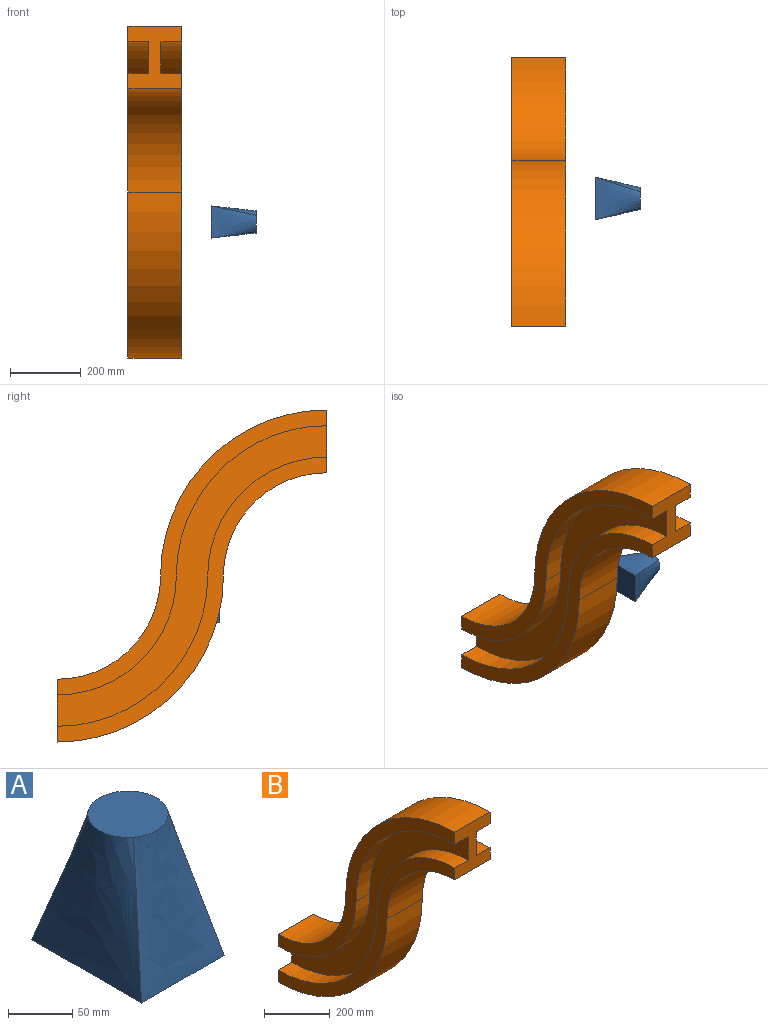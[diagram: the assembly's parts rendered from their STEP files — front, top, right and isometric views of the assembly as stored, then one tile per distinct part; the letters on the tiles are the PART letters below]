
ASSEMBLY  parts=2 mates=1
PART A: 6 faces, bbox 91.2x120.9x127 mm
  f0: plane 120.89x91.17mm, normal (0,0,-1), area 11021.7mm2, adj f2,f3,f4,f5
  f1: plane 62.63x62.63mm, normal (0,0,1), area 3078mm2, adj f2,f3,f4,f5
  f2: bspline ~127x91.17mm, area 9063.2mm2, adj f0,f1,f3,f5
  f3: bspline ~127x120.89mm, area 10768.1mm2, adj f0,f1,f2,f4
  f4: bspline ~127x91.17mm, area 9063.2mm2, adj f0,f1,f3,f5
  f5: bspline ~127x120.89mm, area 10768.1mm2, adj f0,f1,f2,f4
PART B: 20 faces, bbox 152.4x762x939.8 mm
  f0: plane 177.8x152.4mm, normal (0,-1,0), area 16637.6mm2, adj f2,f3,f4,f5,f6,f7,f8,f9
  f1: plane 177.8x152.4mm, normal (0,1,0), area 16637.6mm2, adj f3,f5,f7,f9,f11,f13,f14,f15
  f2: cylinder r=425.45mm len=425.45mm, axis (-1,0,0), area 39312.6mm2, adj f0,f3,f13,f14
  f3: plane 806.45x762mm, normal (-1,0,0), area 53204.3mm2, adj f0,f1,f2,f4,f14,f15
  f4: cylinder r=469.9mm len=469.9mm, axis (-1,0,0), area 112489.1mm2, adj f0,f3,f5,f15
  f5: plane 806.45x762mm, normal (1,0,0), area 53204.3mm2, adj f0,f1,f4,f6,f15,f16
  f6: cylinder r=425.45mm len=425.45mm, axis (-1,0,0), area 39312.6mm2, adj f0,f5,f7,f16
  f7: plane 850.9x762mm, normal (1,0,0), area 106408.6mm2, adj f0,f1,f6,f8,f16,f17
  f8: cylinder r=336.55mm len=336.55mm, axis (-1,0,0), area 31098mm2, adj f0,f7,f9,f17
  f9: plane 806.45x762mm, normal (1,0,0), area 53204.3mm2, adj f0,f1,f8,f10,f17,f18
  f10: cylinder r=292.1mm len=292.1mm, axis (-1,0,0), area 69925.6mm2, adj f0,f9,f11,f18
  f11: plane 806.45x762mm, normal (-1,0,0), area 53204.3mm2, adj f0,f1,f10,f12,f18,f19
  f12: cylinder r=336.55mm len=336.55mm, axis (-1,0,0), area 31098mm2, adj f0,f11,f13,f19
  f13: plane 850.9x762mm, normal (-1,0,0), area 106408.6mm2, adj f0,f1,f2,f12,f14,f19
  f14: cylinder r=336.55mm len=336.55mm, axis (1,0,0), area 31098mm2, adj f1,f2,f3,f13
  f15: cylinder r=292.1mm len=292.1mm, axis (1,0,0), area 69925.6mm2, adj f1,f3,f4,f5
  f16: cylinder r=336.55mm len=336.55mm, axis (1,0,0), area 31098mm2, adj f1,f5,f6,f7
  f17: cylinder r=425.45mm len=425.45mm, axis (1,0,0), area 39312.6mm2, adj f1,f7,f8,f9
  f18: cylinder r=469.9mm len=469.9mm, axis (1,0,0), area 112489.1mm2, adj f1,f9,f10,f11
  f19: cylinder r=425.45mm len=425.45mm, axis (1,0,0), area 39312.6mm2, adj f1,f11,f12,f13
PLACE A rot(axis=(0,1,0),90deg) t=(286.66,485.45,-433.73)mm
PLACE B t=(127,122.67,32.16)mm fixed
MATE slider B.f9 <-> A.f1  axis (1,0,0) through (203.2,485.45,-433.73)mm
